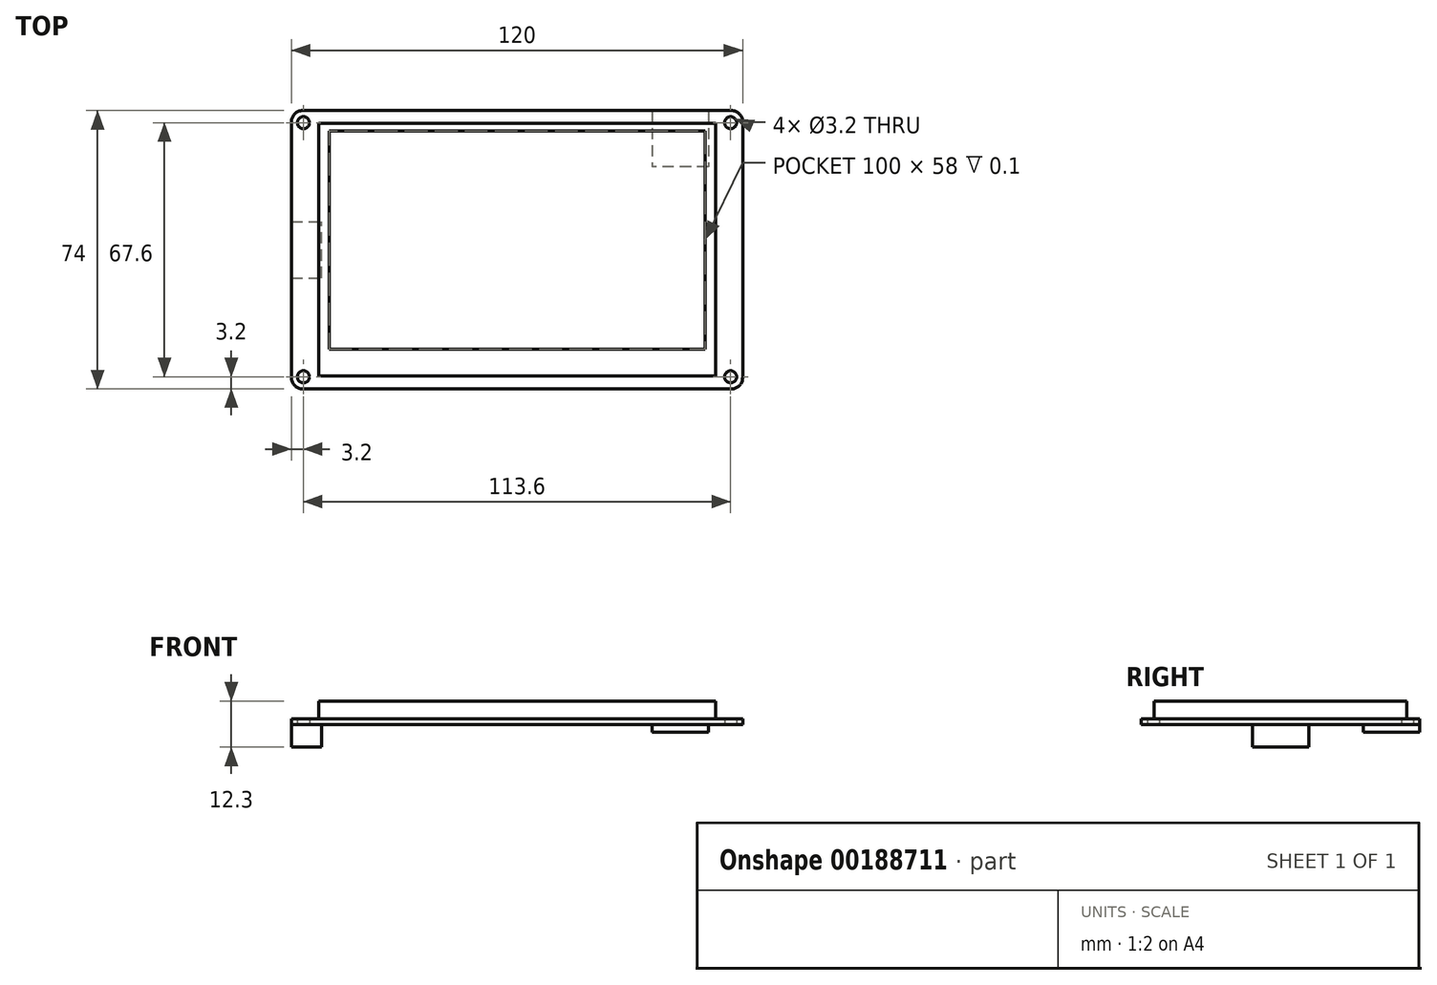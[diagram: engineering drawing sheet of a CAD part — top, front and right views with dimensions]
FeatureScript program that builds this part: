
annotation { "Feature Type Name" : "Feature", "Feature Type Description" : "" }
export const myFeature = defineFeature(function(context is Context, id is Id, definition is map)
    precondition{}
    {
        {
            var Q0;
            Q0=qCreatedBy(makeId("Top.planeOp"),FACE);
            var sketch = newSketch(context, id + "F0", { "sketchPlane" : qUnion([Q0])});
            skLineSegment(sketch, "E0.bottom", {"start": v(60, -37) * mm, "end": v(-60, -37) * mm});
            skLineSegment(sketch, "E0.top", {"start": v(60, 37) * mm, "end": v(-60, 37) * mm});
            skLineSegment(sketch, "E0.left", {"start": v(60, -37) * mm, "end": v(60, 37) * mm});
            skLineSegment(sketch, "E0.right", {"start": v(-60, -37) * mm, "end": v(-60, 37) * mm});
            skPoint(sketch, "E0.middle", {"position": v(0, 0) * mm});
            skLineSegment(sketch, "E1.bottom", {"start": v(56.8, 33.8) * mm, "end": v(-56.8, 33.8) * mm, "construction": true});
            skLineSegment(sketch, "E1.top", {"start": v(56.8, -33.8) * mm, "end": v(-56.8, -33.8) * mm, "construction": true});
            skLineSegment(sketch, "E1.left", {"start": v(56.8, 33.8) * mm, "end": v(56.8, -33.8) * mm, "construction": true});
            skLineSegment(sketch, "E1.right", {"start": v(-56.8, 33.8) * mm, "end": v(-56.8, -33.8) * mm, "construction": true});
            skCircle(sketch, "E2", {"center": v(-56.8, 33.8) * mm, "radius": 1.6 * mm});
            skCircle(sketch, "E3", {"center": v(-56.8, -33.8) * mm, "radius": 1.6 * mm});
            skCircle(sketch, "E4", {"center": v(56.8, 33.8) * mm, "radius": 1.6 * mm});
            skCircle(sketch, "E5", {"center": v(56.8, -33.8) * mm, "radius": 1.6 * mm});
            skSolve(sketch);
        }
        {
            var Q0;
            Q0=makeQuery(id+"F0.imprint","IMPRINT",FACE,{"disambiguationData":[TD([[makeQuery(id+"F0.imprint","IMPRINT",EDGE,{"derivedFrom":sQuery(id+"F0.wireOp",EDGE,"E0.bottom")}),-1.0]])]});
            extrude(context, id + "F1", {"entities" : qUnion([Q0]), "depth" : 1.6 * mm});
        }
        {
            var Q0;
            Q0=makeQuery(id+"F1.opExtrude","CAP_FACE",FACE,{"disambiguationData":[OSD([sQuery(id+"F0.wireOp",EDGE,"E0.bottom"),sQuery(id+"F0.wireOp",EDGE,"E0.top"),sQuery(id+"F0.wireOp",EDGE,"E0.left"),sQuery(id+"F0.wireOp",EDGE,"E0.right"),sQuery(id+"F0.wireOp",EDGE,"E2"),sQuery(id+"F0.wireOp",EDGE,"E3"),sQuery(id+"F0.wireOp",EDGE,"E4"),sQuery(id+"F0.wireOp",EDGE,"E5")])],"isStart":false});
            var sketch = newSketch(context, id + "F2", { "sketchPlane" : qUnion([Q0])});
            skLineSegment(sketch, "E6.bottom", {"start": v(-52.75, 33.6) * mm, "end": v(52.75, 33.6) * mm});
            skLineSegment(sketch, "E6.top", {"start": v(-52.75, -33.6) * mm, "end": v(52.75, -33.6) * mm});
            skLineSegment(sketch, "E6.left", {"start": v(-52.75, 33.6) * mm, "end": v(-52.75, -33.6) * mm});
            skLineSegment(sketch, "E6.right", {"start": v(52.75, 33.61) * mm, "end": v(52.75, -33.6) * mm});
            skLineSegment(sketch, "E7", {"start": v(0, 33.6) * mm, "end": v(0, 0) * mm, "construction": true});
            skSolve(sketch);
        }
        {
            var Q0;
            Q0=makeQuery(id+"F2.imprint","IMPRINT",FACE,{"disambiguationData":[TD([[makeQuery(id+"F2.imprint","IMPRINT",EDGE,{"derivedFrom":sQuery(id+"F2.wireOp",EDGE,"E6.bottom")}),-1.0]])]});
            extrude(context, id + "F3", {"entities" : qUnion([Q0]), "operationType" : NewBodyOperationType.ADD, "depth" : 4.7 * mm});
        }
        {
            var Q0;
            Q0=makeQuery(id+"F3.opExtrude","CAP_FACE",FACE,{"disambiguationData":[OSD([sQuery(id+"F2.wireOp",EDGE,"E6.bottom"),sQuery(id+"F2.wireOp",EDGE,"E6.top"),sQuery(id+"F2.wireOp",EDGE,"E6.left"),sQuery(id+"F2.wireOp",EDGE,"E6.right")])],"isStart":false});
            var sketch = newSketch(context, id + "F4", { "sketchPlane" : qUnion([Q0])});
            skLineSegment(sketch, "E8.bottom", {"start": v(-50, 31.6) * mm, "end": v(50, 31.6) * mm});
            skLineSegment(sketch, "E8.top", {"start": v(-50, -26.4) * mm, "end": v(50, -26.4) * mm});
            skLineSegment(sketch, "E8.left", {"start": v(-50, 31.6) * mm, "end": v(-50, -26.4) * mm});
            skLineSegment(sketch, "E8.right", {"start": v(50, 31.6) * mm, "end": v(50, -26.4) * mm});
            skLineSegment(sketch, "E9", {"start": v(0, 31.6) * mm, "end": v(0, 0) * mm, "construction": true});
            skSolve(sketch);
        }
        {
            var Q0;
            Q0=qSketchRegion(id+"F4",true);
            extrude(context, id + "F5", {"entities" : qUnion([Q0]), "operationType" : NewBodyOperationType.REMOVE, "oppositeDirection" : true, "depth" : .1 * mm});
        }
        {
            var Q0;
            Q0=makeQuery(id+"F1.opExtrude","CAP_FACE",FACE,{"disambiguationData":[OSD([sQuery(id+"F0.wireOp",EDGE,"E0.bottom"),sQuery(id+"F0.wireOp",EDGE,"E0.top"),sQuery(id+"F0.wireOp",EDGE,"E0.left"),sQuery(id+"F0.wireOp",EDGE,"E0.right"),sQuery(id+"F0.wireOp",EDGE,"E2"),sQuery(id+"F0.wireOp",EDGE,"E3"),sQuery(id+"F0.wireOp",EDGE,"E4"),sQuery(id+"F0.wireOp",EDGE,"E5")])],"isStart":true});
            var sketch = newSketch(context, id + "F6", { "sketchPlane" : qUnion([Q0])});
            skLineSegment(sketch, "E10.bottom", {"start": v(50.87, -37) * mm, "end": v(35.87, -37) * mm});
            skLineSegment(sketch, "E10.top", {"start": v(50.87, -22) * mm, "end": v(35.87, -22) * mm});
            skLineSegment(sketch, "E10.left", {"start": v(50.87, -37) * mm, "end": v(50.87, -22) * mm});
            skLineSegment(sketch, "E10.right", {"start": v(35.87, -37) * mm, "end": v(35.87, -22) * mm});
            skLineSegment(sketch, "E11.bottom", {"start": v(-60, 7.5) * mm, "end": v(-52, 7.5) * mm});
            skLineSegment(sketch, "E11.top", {"start": v(-60, -7.5) * mm, "end": v(-52, -7.5) * mm});
            skLineSegment(sketch, "E11.left", {"start": v(-60, 7.5) * mm, "end": v(-60, -7.5) * mm});
            skLineSegment(sketch, "E11.right", {"start": v(-52, 7.5) * mm, "end": v(-52, -7.5) * mm});
            skPoint(sketch, "E12", {"position": v(-52, 0) * mm});
            skSolve(sketch);
        }
        {
            var Q0;
            Q0=makeQuery(id+"F6.imprint","IMPRINT",FACE,{"disambiguationData":[TD([[makeQuery(id+"F6.imprint","IMPRINT",EDGE,{"derivedFrom":sQuery(id+"F6.wireOp",EDGE,"E10.bottom")}),-1.0]])]});
            extrude(context, id + "F7", {"entities" : qUnion([Q0]), "operationType" : NewBodyOperationType.ADD, "depth" : 2 * mm});
        }
        {
            var Q0;
            Q0=makeQuery(id+"F6.imprint","IMPRINT",FACE,{"disambiguationData":[TD([[makeQuery(id+"F6.imprint","IMPRINT",EDGE,{"derivedFrom":sQuery(id+"F6.wireOp",EDGE,"E11.bottom")}),-1.0]])]});
            extrude(context, id + "F8", {"entities" : qUnion([Q0]), "operationType" : NewBodyOperationType.ADD, "depth" : 6 * mm});
        }
        {
            var Q0;
            Q0=makeQuery(id+"F1.opExtrude","SWEPT_EDGE",EDGE,{"disambiguationData":[OSD([sQuery(id+"F0.wireOp",EDGE,"E0.top"),sQuery(id+"F0.wireOp",EDGE,"E0.left")])]});
            var Q1;
            Q1=makeQuery(id+"F1.opExtrude","SWEPT_EDGE",EDGE,{"disambiguationData":[OSD([sQuery(id+"F0.wireOp",EDGE,"E0.bottom"),sQuery(id+"F0.wireOp",EDGE,"E0.left")])]});
            var Q2;
            Q2=makeQuery(id+"F1.opExtrude","SWEPT_EDGE",EDGE,{"disambiguationData":[OSD([sQuery(id+"F0.wireOp",EDGE,"E0.bottom"),sQuery(id+"F0.wireOp",EDGE,"E0.right")])]});
            var Q3;
            Q3=makeQuery(id+"F1.opExtrude","SWEPT_EDGE",EDGE,{"disambiguationData":[OSD([sQuery(id+"F0.wireOp",EDGE,"E0.top"),sQuery(id+"F0.wireOp",EDGE,"E0.right")])]});
            fillet(context, id + "F9", {"entities" : qUnion([Q0, Q1, Q2, Q3]), "radius" : 3 * mm, "tangentPropagation" : true, "allowEdgeOverflow" : false});
        }
    });
